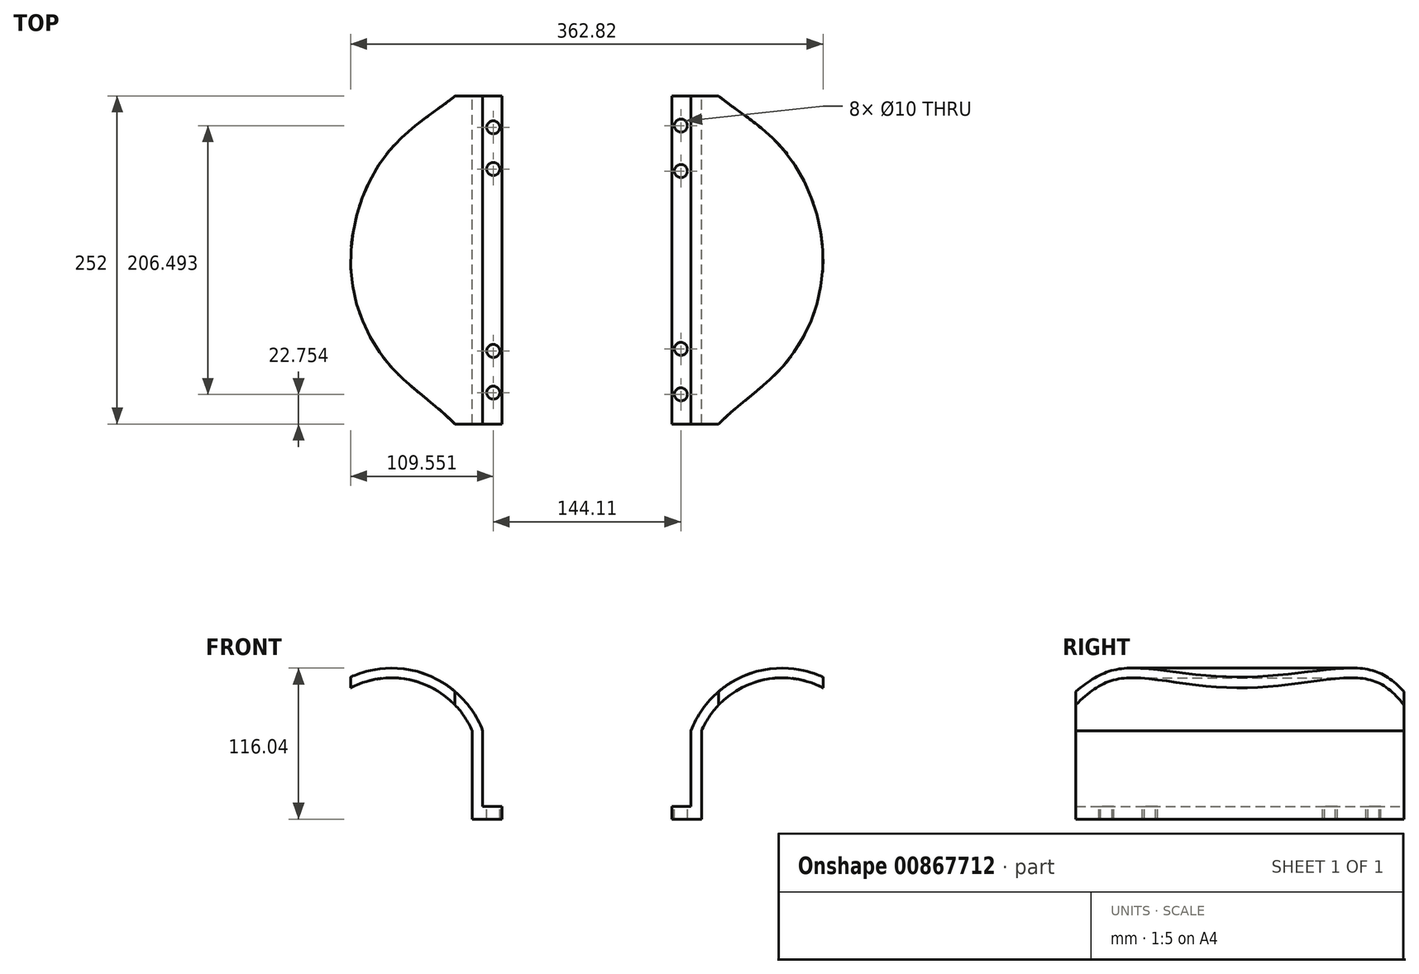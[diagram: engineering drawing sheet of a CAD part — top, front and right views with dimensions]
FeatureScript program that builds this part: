
annotation { "Feature Type Name" : "Feature", "Feature Type Description" : "" }
export const myFeature = defineFeature(function(context is Context, id is Id, definition is map)
    precondition{}
    {
        {
            var Q0;
            Q0=qCreatedBy(makeId("Front.planeOp"),FACE);
            var sketch = newSketch(context, id + "F0", { "sketchPlane" : qUnion([Q0])});
            skArc(sketch, "E0", {"start": v(70.04, 26.81) * mm, "mid": v(25.75, 70.44) * mm, "end": v(-36.25, 65.66) * mm});
            skArc(sketch, "E1", {"start": v(61.95, 26.81) * mm, "mid": v(19.8, 64.53) * mm, "end": v(-36.25, 56.94) * mm});
            skPoint(sketch, "E2.orphan", {"position": v(-71.4, 0) * mm});
            skLineSegment(sketch, "E3.trimOffspring", {"start": v(70.04, -12.74) * mm, "end": v(73.79, -13.42) * mm});
            skLineSegment(sketch, "E4", {"start": v(-36.25, 56.94) * mm, "end": v(-36.25, 65.66) * mm});
            skLineSegment(sketch, "E5", {"start": v(61.95, 26.81) * mm, "end": v(61.95, -41.04) * mm});
            skLineSegment(sketch, "E6", {"start": v(70.04, 26.81) * mm, "end": v(70.04, -31.34) * mm});
            skLineSegment(sketch, "E7.bottom", {"start": v(61.95, -41.04) * mm, "end": v(84.83, -41.04) * mm});
            skLineSegment(sketch, "E7.top", {"start": v(70.04, -31.34) * mm, "end": v(84.83, -31.34) * mm});
            skLineSegment(sketch, "E7.left", {"start": v(61.95, -41.04) * mm, "end": v(61.95, -31.34) * mm});
            skPoint(sketch, "E8.orphan", {"position": v(99.61, -11.3) * mm});
            skPoint(sketch, "E9.orphan", {"position": v(70.04, -41.04) * mm});
            skLineSegment(sketch, "E10", {"start": v(84.83, -31.34) * mm, "end": v(84.83, -41.04) * mm});
            skPoint(sketch, "E11.orphan", {"position": v(96.95, -41.04) * mm});
            skPoint(sketch, "E12.orphan", {"position": v(99.61, -31.34) * mm});
            skSolve(sketch);
        }
        {
            var Q0;
            Q0 = qSketchRegion(id + "F0", true);
            extrude(context, id + "F1", {"entities" : qUnion([Q0]), "depth" : 126 * mm, "offsetDistance" : 25 * mm, "hasSecondDirection" : true, "secondDirectionOppositeDirection" : true, "secondDirectionDepth" : 126 * mm});
        }
        {
            var Q0;
            Q0=qCreatedBy(makeId("Right.planeOp"),FACE);
            cPlane(context, id + "F2", {"entities" : qUnion([Q0]), "cplaneType" : CPlaneType.OFFSET, "offset" : 150 * mm, "width" : 150 * mm, "height" : 150 * mm});
        }
        {
            var Q0;
            Q0=makeQuery(id+"F1.opExtrude","SWEPT_BODY",BODY,{"disambiguationData":[OSD([sQuery(id+"F0.wireOp",EDGE,"E0"),sQuery(id+"F0.wireOp",EDGE,"E1"),sQuery(id+"F0.wireOp",EDGE,"qXNlpBPX-BT0N-w7rS-HwOe-rPGnPSx8J7Nq"),sQuery(id+"F0.wireOp",EDGE,"gEJxzdbX-Chy3-PRoj-Tsgt-ZlCudkSS9O1N.bottom"),sQuery(id+"F0.wireOp",EDGE,"gEJxzdbX-Chy3-PRoj-Tsgt-ZlCudkSS9O1N.top"),sQuery(id+"F0.wireOp",EDGE,"gEJxzdbX-Chy3-PRoj-Tsgt-ZlCudkSS9O1N.right")])]});
            var Q1;
            Q1=qCreatedBy(id+"F2.planeOp",FACE);
            mirror(context, id + "F3", {"entities" : qUnion([Q0]), "mirrorPlane" : qUnion([Q1])});
        }
        {
            var Q0;
            Q0=qCreatedBy(makeId("Top.planeOp"),FACE);
            var sketch = newSketch(context, id + "F4", { "sketchPlane" : qUnion([Q0])});
            skFitSpline(sketch, "E13", {"points": [v(59.6, -139.94) * mm, v(0, -82.46) * mm, v(-31.4, 0) * mm, v(0, 85.98) * mm, v(58.8, 134.67) * mm, v(73.17, 175.39) * mm, v(-142.98, 165.8) * mm, v(-269.18, -51.69) * mm, v(-91.97, -181.92) * mm, v(59.6, -192.63) * mm, v(59.6, -139.94) * mm]});
            skSolve(sketch);
        }
        {
            var Q0;
            Q0 = qSketchRegion(id + "F4", true);
            extrude(context, id + "F5", {"entities" : qUnion([Q0]), "operationType" : NewBodyOperationType.REMOVE, "depth" : 100 * mm, "offsetDistance" : 25 * mm});
        }
        {
            var Q0;
            Q0=makeQuery(id+"F3.opPattern","COPY",BODY,{"derivedFrom":makeQuery(id+"F1.opExtrude","SWEPT_BODY",BODY,{"disambiguationData":[OSD([sQuery(id+"F0.wireOp",EDGE,"E0"),sQuery(id+"F0.wireOp",EDGE,"E1"),sQuery(id+"F0.wireOp",EDGE,"gEJxzdbX-Chy3-PRoj-Tsgt-ZlCudkSS9O1N.bottom"),sQuery(id+"F0.wireOp",EDGE,"gEJxzdbX-Chy3-PRoj-Tsgt-ZlCudkSS9O1N.top"),sQuery(id+"F0.wireOp",EDGE,"gEJxzdbX-Chy3-PRoj-Tsgt-ZlCudkSS9O1N.right"),sQuery(id+"F0.wireOp",EDGE,"E4")])]}),"instanceName":"1"});
            deleteBodies(context, id + "F6", {"entities" : qUnion([Q0])});
        }
        {
            var Q0;
            Q0=makeQuery(id+"F1.opExtrude","SWEPT_BODY",BODY,{"disambiguationData":[OSD([sQuery(id+"F0.wireOp",EDGE,"E0"),sQuery(id+"F0.wireOp",EDGE,"E1"),sQuery(id+"F0.wireOp",EDGE,"E4"),sQuery(id+"F0.wireOp",EDGE,"E5"),sQuery(id+"F0.wireOp",EDGE,"E6"),sQuery(id+"F0.wireOp",EDGE,"E7.bottom"),sQuery(id+"F0.wireOp",EDGE,"E7.top"),sQuery(id+"F0.wireOp",EDGE,"E7.left"),sQuery(id+"F0.wireOp",EDGE,"E10")])]});
            var Q1;
            Q1=qCreatedBy(id+"F2.planeOp",FACE);
            mirror(context, id + "F7", {"entities" : qUnion([Q0]), "mirrorPlane" : qUnion([Q1])});
        }
        {
            var Q0;
            Q0=makeQuery(id+"F1.opExtrude","SWEPT_FACE",FACE,{"disambiguationData":[OSD([sQuery(id+"F0.wireOp",EDGE,"E7.top")])]});
            var sketch = newSketch(context, id + "F8", { "sketchPlane" : qUnion([Q0])});
            skCircle(sketch, "E14", {"center": v(78.14, -101.91) * mm, "radius": 5 * mm});
            skCircle(sketch, "E15", {"center": v(78.14, -69.91) * mm, "radius": 5 * mm});
            skCircle(sketch, "E16.MirrorC", {"center": v(78.14, 69.91) * mm, "radius": 5 * mm});
            skCircle(sketch, "E17.MirrorC", {"center": v(78.14, 101.91) * mm, "radius": 5 * mm});
            skSolve(sketch);
        }
        {
            var Q0;
            Q0 = qSketchRegion(id + "F8", true);
            extrude(context, id + "F9", {"entities" : qUnion([Q0]), "operationType" : NewBodyOperationType.REMOVE, "oppositeDirection" : true, "depth" : 25 * mm, "offsetDistance" : 25 * mm});
        }
        {
            var Q0;
            Q0=makeQuery(id+"F7.opPattern","COPY",FACE,{"derivedFrom":makeQuery(id+"F1.opExtrude","SWEPT_FACE",FACE,{"disambiguationData":[OSD([sQuery(id+"F0.wireOp",EDGE,"E7.top")])]}),"instanceName":"1"});
            var sketch = newSketch(context, id + "F10", { "sketchPlane" : qUnion([Q0])});
            skCircle(sketch, "E18", {"center": v(222.25, -103.25) * mm, "radius": 5 * mm});
            skCircle(sketch, "E19", {"center": v(222.25, -68.31) * mm, "radius": 5 * mm});
            skCircle(sketch, "E20.MirrorC", {"center": v(222.25, 68.31) * mm, "radius": 5 * mm});
            skCircle(sketch, "E21.MirrorC", {"center": v(222.25, 103.25) * mm, "radius": 5 * mm});
            skSolve(sketch);
        }
        {
            var Q0;
            Q0 = qSketchRegion(id + "F10", true);
            extrude(context, id + "F11", {"entities" : qUnion([Q0]), "operationType" : NewBodyOperationType.REMOVE, "oppositeDirection" : true, "depth" : 25 * mm, "offsetDistance" : 25 * mm});
        }
    });
